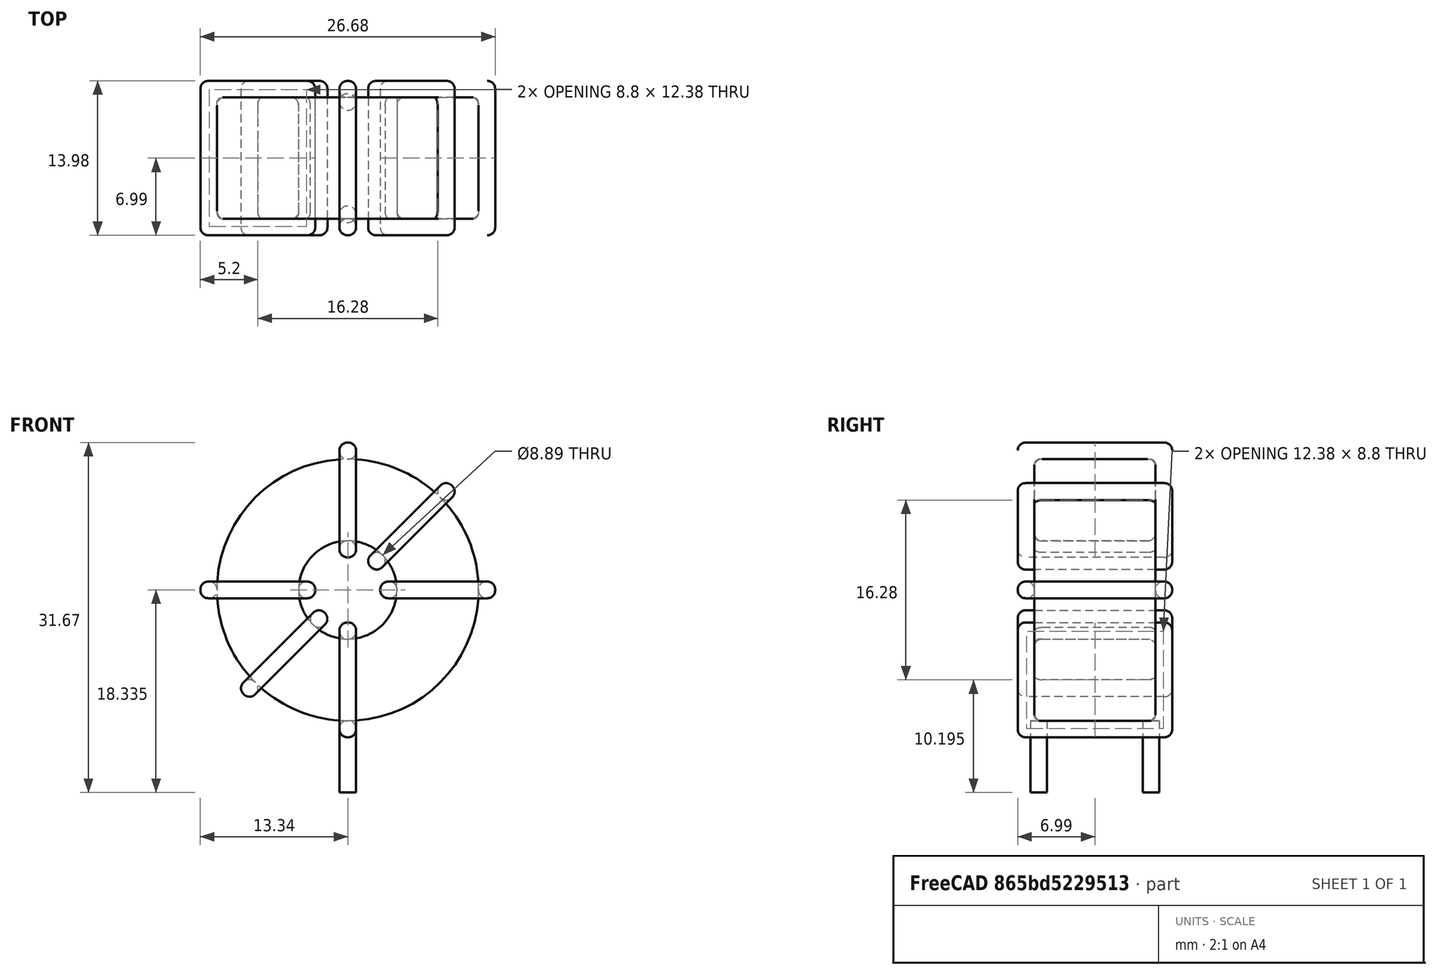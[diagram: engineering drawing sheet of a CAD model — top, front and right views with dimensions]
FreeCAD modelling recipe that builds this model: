
FCSTD DOCUMENT  (FreeCAD 0.16R6703 (Git))
Label: L_Toroid_Vertical_L26.7mm_W14.0mm_P10.16mm_Pulse_D
License: All rights reserved
LicenseURL: http://en.wikipedia.org/wiki/All_rights_reserved
objects: Sketcher::SketchObject×6, PartDesign::Pad×6, PartDesign::Fillet×5, Spreadsheet::Sheet×1
note: 23 computed .brp shape members not serialized (recipe doc carries the construction recipe); baked Part::Feature solids carry a one-line shape summary decoded from their .brp

FEATURE [Spreadsheet::Sheet] Spreadsheet  label="dimensions"
  cells = A1=Wx; B1(Wx)=26.67; C1(WW)=8.890000000000001; D1=26.67; A2=Wy; B2(Wy)=13.97; D2=13.97; A3=RM; B3(RMx)=10.16; C3(RMy)=0; A4=d_wire; B4(d_wire)=1.5; A5=H; B5(H)=26.67; A6=offsetx; B6(offsetx)=13.335
FEATURE [Sketcher::SketchObject] Sketch
  Placement = pos=(0,-5.08,0) rot=(1,0,0;1.5708rad)
  expr: Placement.Base.y = -Spreadsheet.RMx / 2
  expr: Constraints[0] = Spreadsheet.Wx / 2 - Spreadsheet.d_wire
  expr: Constraints[4] = Spreadsheet.WW / 2
  expr: Constraints[2] = Spreadsheet.Wx / 2 + Spreadsheet.d_wire + 0.5
  sketch-geometry (2):
    g0: Circle CenterX=0 CenterY=15.335 CenterZ=0 NormalX=0 NormalY=0 NormalZ=1 Radius=11.835
    g1: Circle CenterX=0 CenterY=15.335 CenterZ=0 NormalX=0 NormalY=0 NormalZ=1 Radius=4.445
  constraints (5):
    c: Radius(g0) = 11.835
    c: DistanceX(g-1,g0) = 0
    c: DistanceY(g-1,g0) = 15.335
    c: Coincident(g1,g0)
    c: Radius(g1) = 4.445
FEATURE [PartDesign::Pad] Pad
  Length = 10.97
  Length2 = 100
  Midplane = true
  Placement = pos=(0,-5.08,0) rot=(1,0,0;1.5708rad)
  Sketch = -> Sketch
  Type = 0
  expr: Length = Spreadsheet.Wy - 2 * Spreadsheet.d_wire
FEATURE [Sketcher::SketchObject] Sketch001
  Placement = pos=(0,0,2) rot=(0,0,1;0rad)
  expr: Placement.Base.z = 0.5 + Spreadsheet.d_wire
  expr: Constraints[4] = Spreadsheet.RMy
  expr: Constraints[2] = -Spreadsheet.RMx
  expr: Constraints[1] = Spreadsheet.d_wire / 2
  sketch-geometry (2):
    g0: Circle CenterX=0 CenterY=0 CenterZ=0 NormalX=0 NormalY=0 NormalZ=1 Radius=0.75
    g1: Circle CenterX=0 CenterY=-10.16 CenterZ=0 NormalX=0 NormalY=0 NormalZ=1 Radius=0.75
  constraints (5):
    c: Equal(g0,g1)
    c: Radius(g0) = 0.75
    c: DistanceY(g-1,g1) = -10.16
    c: Coincident(g0,g-1)
    c: DistanceX(g-1,g1) = 0
FEATURE [PartDesign::Pad] Pad001
  Length = 1.5
  Length2 = 5
  Placement = pos=(0,0,2) rot=(0,0,1;0rad)
  Reversed = true
  Sketch = -> Sketch001
  Type = 4
  expr: Length2 = 3.5 + Spreadsheet.d_wire
  expr: Length = Spreadsheet.d_wire
FEATURE [PartDesign::Fillet] Fillet
  Base = -> Pad [Edge6,Edge3,Edge2]
  Placement = pos=(0,-5.08,0) rot=(1,0,0;1.5708rad)
  Radius = 0.5
FEATURE [Sketcher::SketchObject] Sketch003
  Placement = pos=(0,1.905,15.335) rot=(1,0,0;3.14159rad)
  expr: Constraints[18] = Spreadsheet.d_wire
  expr: Constraints[16] = Spreadsheet.d_wire
  expr: Constraints[19] = Spreadsheet.d_wire
  expr: Constraints[17] = Spreadsheet.d_wire
  expr: Placement.Base.y = -1 * (Spreadsheet.RMx - Spreadsheet.Wy) / 2
  expr: Constraints[21] = (Spreadsheet.Wx - Spreadsheet.WW) / 2 - Spreadsheet.d_wire
  expr: Constraints[22] = Spreadsheet.Wx / 2 - Spreadsheet.d_wire
  expr: Constraints[43] = Spreadsheet.d_wire
  expr: Constraints[48] = Spreadsheet.Wx - Spreadsheet.d_wire * 2
  expr: Constraints[49] = Spreadsheet.Wy
  expr: Placement.Base.z = Spreadsheet.Wx / 2 + Spreadsheet.d_wire + 0.5
  sketch-geometry (16):
    g0: LineSegment StartX=-2.945 StartY=0 StartZ=0 EndX=-13.335 EndY=0 EndZ=0
    g1: LineSegment StartX=-13.335 StartY=0 StartZ=0 EndX=-13.335 EndY=13.97 EndZ=0
    g2: LineSegment StartX=-13.335 StartY=13.97 StartZ=0 EndX=-2.945 EndY=13.97 EndZ=0
    g3: LineSegment StartX=-2.945 StartY=13.97 StartZ=0 EndX=-2.945 EndY=0 EndZ=0
    g4: LineSegment StartX=-11.835 StartY=12.47 StartZ=0 EndX=-4.445 EndY=12.47 EndZ=0
    g5: LineSegment StartX=-4.445 StartY=12.47 StartZ=0 EndX=-4.445 EndY=1.5 EndZ=0
    g6: LineSegment StartX=-4.445 StartY=1.5 StartZ=0 EndX=-11.835 EndY=1.5 EndZ=0
    g7: LineSegment StartX=-11.835 StartY=1.5 StartZ=0 EndX=-11.835 EndY=12.47 EndZ=0
    g8: LineSegment StartX=2.945 StartY=13.97 StartZ=0 EndX=13.335 EndY=13.97 EndZ=0
    g9: LineSegment StartX=13.335 StartY=13.97 StartZ=0 EndX=13.335 EndY=0 EndZ=0
    g10: LineSegment StartX=13.335 StartY=0 StartZ=0 EndX=2.945 EndY=0 EndZ=0
    g11: LineSegment StartX=2.945 StartY=0 StartZ=0 EndX=2.945 EndY=13.97 EndZ=0
    g12: LineSegment StartX=4.445 StartY=12.47 StartZ=0 EndX=11.835 EndY=12.47 EndZ=0
    g13: LineSegment StartX=11.835 StartY=12.47 StartZ=0 EndX=11.835 EndY=1.5 EndZ=0
    g14: LineSegment StartX=11.835 StartY=1.5 StartZ=0 EndX=4.445 EndY=1.5 EndZ=0
    g15: LineSegment StartX=4.445 StartY=1.5 StartZ=0 EndX=4.445 EndY=12.47 EndZ=0
  constraints (50):
    c: Horizontal(g0)
    c: Coincident(g1,g0)
    c: Vertical(g1)
    c: Coincident(g2,g1)
    c: Horizontal(g2)
    c: Coincident(g3,g2)
    c: Coincident(g3,g0)
    c: Vertical(g3)
    c: Coincident(g4,g5)
    c: Coincident(g5,g6)
    c: Coincident(g6,g7)
    c: Coincident(g7,g4)
    c: Horizontal(g4)
    c: Horizontal(g6)
    c: Vertical(g5)
    c: Vertical(g7)
    c: DistanceX(g1,g4) = 1.5
    c: DistanceY(g4,g1) = 1.5
    c: DistanceX(g5,g0) = 1.5
    c: DistanceY(g0,g5) = 1.5
    c: DistanceY(g-1,g0) = 0
    c: DistanceX(g6,g6) = 7.39
    c: DistanceX(g6,g-1) = 11.835
    c: Coincident(g8,g9)
    c: Coincident(g9,g10)
    c: Coincident(g10,g11)
    c: Coincident(g11,g8)
    c: Horizontal(g8)
    c: Horizontal(g10)
    c: Vertical(g9)
    c: Vertical(g11)
    c: Coincident(g12,g13)
    c: Coincident(g13,g14)
    c: Coincident(g14,g15)
    c: Coincident(g15,g12)
    c: Horizontal(g12)
    c: Horizontal(g14)
    c: Vertical(g13)
    c: Vertical(g15)
    c: DistanceY(g8,g2) = 0
    c: DistanceY(g10,g0) = 0
    c: DistanceY(g14,g5) = 0
    c: DistanceY(g12,g4) = 0
    c: DistanceX(g8,g12) = 1.5
    c: Equal(g8,g2)
    c: Equal(g12,g4)
    c: Equal(g9,g1)
    c: Equal(g13,g7)
    c: DistanceX(g4,g12) = 23.67
    c: DistanceY(g0,g1) = 13.97
FEATURE [PartDesign::Pad] Pad002
  Length = 1.5
  Length2 = 100
  Midplane = true
  Placement = pos=(0,1.905,15.335) rot=(1,0,0;3.14159rad)
  Sketch = -> Sketch003
  Type = 0
  expr: Length = Spreadsheet.d_wire
FEATURE [PartDesign::Fillet] Fillet001
  Base = -> Pad002 [Edge38,Edge41,Edge42,Edge43,Edge29,Edge32,Edge33,Edge34,Edge25,Edge35,Edge36,Edge13,Edge14,Edge15,Edge16,Edge17,Edge18,Edge19,Edge1,Edge2,Edge3,Edge4,Edge5,Edge6,Edge7,Edge37,Edge39,Edge40,Edge20,Edge23,Edge24,Edge21,Edge22,Edge8,Edge9,Edge10,Edge11,Edge12,Edge26,Edge27,+8 more]
  Placement = pos=(0,1.905,15.335) rot=(1,0,0;3.14159rad)
  Radius = 0.705
  expr: Radius = Spreadsheet.d_wire * 0.47
FEATURE [Sketcher::SketchObject] Sketch004
  Placement = pos=(0,1.905,15.335) rot=(0.92388,0,0.382683;3.14159rad)
  expr: Constraints[18] = Spreadsheet.d_wire
  expr: Constraints[16] = Spreadsheet.d_wire
  expr: Constraints[19] = Spreadsheet.d_wire
  expr: Constraints[17] = Spreadsheet.d_wire
  expr: Placement.Base.y = -1 * (Spreadsheet.RMx - Spreadsheet.Wy) / 2
  expr: Constraints[21] = (Spreadsheet.Wx - Spreadsheet.WW) / 2 - Spreadsheet.d_wire
  expr: Constraints[22] = Spreadsheet.Wx / 2 - Spreadsheet.d_wire
  expr: Constraints[43] = Spreadsheet.d_wire
  expr: Constraints[48] = Spreadsheet.Wx - 2 * Spreadsheet.d_wire
  expr: Constraints[49] = Spreadsheet.Wy
  expr: Placement.Base.z = Spreadsheet.Wx / 2 + Spreadsheet.d_wire + 0.5
  sketch-geometry (16):
    g0: LineSegment StartX=-2.945 StartY=0 StartZ=0 EndX=-13.335 EndY=0 EndZ=0
    g1: LineSegment StartX=-13.335 StartY=0 StartZ=0 EndX=-13.335 EndY=13.97 EndZ=0
    g2: LineSegment StartX=-13.335 StartY=13.97 StartZ=0 EndX=-2.945 EndY=13.97 EndZ=0
    g3: LineSegment StartX=-2.945 StartY=13.97 StartZ=0 EndX=-2.945 EndY=0 EndZ=0
    g4: LineSegment StartX=-11.835 StartY=12.47 StartZ=0 EndX=-4.445 EndY=12.47 EndZ=0
    g5: LineSegment StartX=-4.445 StartY=12.47 StartZ=0 EndX=-4.445 EndY=1.5 EndZ=0
    g6: LineSegment StartX=-4.445 StartY=1.5 StartZ=0 EndX=-11.835 EndY=1.5 EndZ=0
    g7: LineSegment StartX=-11.835 StartY=1.5 StartZ=0 EndX=-11.835 EndY=12.47 EndZ=0
    g8: LineSegment StartX=2.945 StartY=13.97 StartZ=0 EndX=13.335 EndY=13.97 EndZ=0
    g9: LineSegment StartX=13.335 StartY=13.97 StartZ=0 EndX=13.335 EndY=0 EndZ=0
    g10: LineSegment StartX=13.335 StartY=0 StartZ=0 EndX=2.945 EndY=0 EndZ=0
    g11: LineSegment StartX=2.945 StartY=0 StartZ=0 EndX=2.945 EndY=13.97 EndZ=0
    g12: LineSegment StartX=4.445 StartY=12.47 StartZ=0 EndX=11.835 EndY=12.47 EndZ=0
    g13: LineSegment StartX=11.835 StartY=12.47 StartZ=0 EndX=11.835 EndY=1.5 EndZ=0
    g14: LineSegment StartX=11.835 StartY=1.5 StartZ=0 EndX=4.445 EndY=1.5 EndZ=0
    g15: LineSegment StartX=4.445 StartY=1.5 StartZ=0 EndX=4.445 EndY=12.47 EndZ=0
  constraints (50):
    c: Horizontal(g0)
    c: Coincident(g1,g0)
    c: Vertical(g1)
    c: Coincident(g2,g1)
    c: Horizontal(g2)
    c: Coincident(g3,g2)
    c: Coincident(g3,g0)
    c: Vertical(g3)
    c: Coincident(g4,g5)
    c: Coincident(g5,g6)
    c: Coincident(g6,g7)
    c: Coincident(g7,g4)
    c: Horizontal(g4)
    c: Horizontal(g6)
    c: Vertical(g5)
    c: Vertical(g7)
    c: DistanceX(g1,g4) = 1.5
    c: DistanceY(g4,g1) = 1.5
    c: DistanceX(g5,g0) = 1.5
    c: DistanceY(g0,g5) = 1.5
    c: DistanceY(g-1,g0) = 0
    c: DistanceX(g6,g6) = 7.39
    c: DistanceX(g6,g-1) = 11.835
    c: Coincident(g8,g9)
    c: Coincident(g9,g10)
    c: Coincident(g10,g11)
    c: Coincident(g11,g8)
    c: Horizontal(g8)
    c: Horizontal(g10)
    c: Vertical(g9)
    c: Vertical(g11)
    c: Coincident(g12,g13)
    c: Coincident(g13,g14)
    c: Coincident(g14,g15)
    c: Coincident(g15,g12)
    c: Horizontal(g12)
    c: Horizontal(g14)
    c: Vertical(g13)
    c: Vertical(g15)
    c: DistanceY(g8,g2) = 0
    c: DistanceY(g10,g0) = 0
    c: DistanceY(g14,g5) = 0
    c: DistanceY(g12,g4) = 0
    c: DistanceX(g8,g12) = 1.5
    c: Equal(g8,g2)
    c: Equal(g12,g4)
    c: Equal(g9,g1)
    c: Equal(g13,g7)
    c: DistanceX(g4,g12) = 23.67
    c: DistanceY(g0,g1) = 13.97
FEATURE [PartDesign::Pad] Pad003
  Length = 1.5
  Length2 = 100
  Midplane = true
  Placement = pos=(0,1.905,15.335) rot=(0.92388,0,0.382683;3.14159rad)
  Sketch = -> Sketch004
  Type = 0
  expr: Length = Spreadsheet.d_wire
FEATURE [PartDesign::Fillet] Fillet002
  Base = -> Pad003 [Edge38,Edge41,Edge42,Edge43,Edge29,Edge32,Edge33,Edge34,Edge25,Edge35,Edge36,Edge13,Edge14,Edge15,Edge16,Edge17,Edge18,Edge19,Edge1,Edge2,Edge3,Edge4,Edge5,Edge6,Edge7,Edge37,Edge39,Edge40,Edge20,Edge23,Edge24,Edge21,Edge22,Edge8,Edge9,Edge10,Edge11,Edge12,Edge26,Edge27,+8 more]
  Placement = pos=(0,1.905,15.335) rot=(0.92388,0,0.382683;3.14159rad)
  Radius = 0.705
  expr: Radius = Spreadsheet.d_wire * 0.47
FEATURE [Sketcher::SketchObject] Sketch005
  Placement = pos=(0,1.905,15.335) rot=(0.92388,0,-0.382683;3.14159rad)
  expr: Constraints[18] = Spreadsheet.d_wire
  expr: Constraints[16] = Spreadsheet.d_wire
  expr: Constraints[19] = Spreadsheet.d_wire
  expr: Constraints[17] = Spreadsheet.d_wire
  expr: Placement.Base.y = -1 * (Spreadsheet.RMx - Spreadsheet.Wy) / 2
  expr: Constraints[21] = (Spreadsheet.Wx - Spreadsheet.WW) / 2 - Spreadsheet.d_wire
  expr: Constraints[22] = Spreadsheet.Wx / 2 - Spreadsheet.d_wire
  expr: Constraints[43] = Spreadsheet.d_wire
  expr: Constraints[48] = Spreadsheet.Wx - 2 * Spreadsheet.d_wire
  expr: Constraints[49] = Spreadsheet.Wy
  expr: Placement.Base.z = Spreadsheet.Wx / 2 + Spreadsheet.d_wire + 0.5
  sketch-geometry (16):
    g0: LineSegment StartX=-2.945 StartY=0 StartZ=0 EndX=-13.335 EndY=0 EndZ=0
    g1: LineSegment StartX=-13.335 StartY=0 StartZ=0 EndX=-13.335 EndY=13.97 EndZ=0
    g2: LineSegment StartX=-13.335 StartY=13.97 StartZ=0 EndX=-2.945 EndY=13.97 EndZ=0
    g3: LineSegment StartX=-2.945 StartY=13.97 StartZ=0 EndX=-2.945 EndY=0 EndZ=0
    g4: LineSegment StartX=-11.835 StartY=12.47 StartZ=0 EndX=-4.445 EndY=12.47 EndZ=0
    g5: LineSegment StartX=-4.445 StartY=12.47 StartZ=0 EndX=-4.445 EndY=1.5 EndZ=0
    g6: LineSegment StartX=-4.445 StartY=1.5 StartZ=0 EndX=-11.835 EndY=1.5 EndZ=0
    g7: LineSegment StartX=-11.835 StartY=1.5 StartZ=0 EndX=-11.835 EndY=12.47 EndZ=0
    g8: LineSegment StartX=2.945 StartY=13.97 StartZ=0 EndX=13.335 EndY=13.97 EndZ=0
    g9: LineSegment StartX=13.335 StartY=13.97 StartZ=0 EndX=13.335 EndY=0 EndZ=0
    g10: LineSegment StartX=13.335 StartY=0 StartZ=0 EndX=2.945 EndY=0 EndZ=0
    g11: LineSegment StartX=2.945 StartY=0 StartZ=0 EndX=2.945 EndY=13.97 EndZ=0
    g12: LineSegment StartX=4.445 StartY=12.47 StartZ=0 EndX=11.835 EndY=12.47 EndZ=0
    g13: LineSegment StartX=11.835 StartY=12.47 StartZ=0 EndX=11.835 EndY=1.5 EndZ=0
    g14: LineSegment StartX=11.835 StartY=1.5 StartZ=0 EndX=4.445 EndY=1.5 EndZ=0
    g15: LineSegment StartX=4.445 StartY=1.5 StartZ=0 EndX=4.445 EndY=12.47 EndZ=0
  constraints (50):
    c: Horizontal(g0)
    c: Coincident(g1,g0)
    c: Vertical(g1)
    c: Coincident(g2,g1)
    c: Horizontal(g2)
    c: Coincident(g3,g2)
    c: Coincident(g3,g0)
    c: Vertical(g3)
    c: Coincident(g4,g5)
    c: Coincident(g5,g6)
    c: Coincident(g6,g7)
    c: Coincident(g7,g4)
    c: Horizontal(g4)
    c: Horizontal(g6)
    c: Vertical(g5)
    c: Vertical(g7)
    c: DistanceX(g1,g4) = 1.5
    c: DistanceY(g4,g1) = 1.5
    c: DistanceX(g5,g0) = 1.5
    c: DistanceY(g0,g5) = 1.5
    c: DistanceY(g-1,g0) = 0
    c: DistanceX(g6,g6) = 7.39
    c: DistanceX(g6,g-1) = 11.835
    c: Coincident(g8,g9)
    c: Coincident(g9,g10)
    c: Coincident(g10,g11)
    c: Coincident(g11,g8)
    c: Horizontal(g8)
    c: Horizontal(g10)
    c: Vertical(g9)
    c: Vertical(g11)
    c: Coincident(g12,g13)
    c: Coincident(g13,g14)
    c: Coincident(g14,g15)
    c: Coincident(g15,g12)
    c: Horizontal(g12)
    c: Horizontal(g14)
    c: Vertical(g13)
    c: Vertical(g15)
    c: DistanceY(g8,g2) = 0
    c: DistanceY(g10,g0) = 0
    c: DistanceY(g14,g5) = 0
    c: DistanceY(g12,g4) = 0
    c: DistanceX(g8,g12) = 1.5
    c: Equal(g8,g2)
    c: Equal(g12,g4)
    c: Equal(g9,g1)
    c: Equal(g13,g7)
    c: DistanceX(g4,g12) = 23.67
    c: DistanceY(g0,g1) = 13.97
FEATURE [PartDesign::Pad] Pad004
  Length = 1.5
  Length2 = 100
  Midplane = true
  Placement = pos=(0,1.905,15.335) rot=(0.92388,0,-0.382683;3.14159rad)
  Sketch = -> Sketch005
  Type = 0
  expr: Length = Spreadsheet.d_wire
FEATURE [PartDesign::Fillet] Fillet003
  Base = -> Pad004 [Edge38,Edge41,Edge42,Edge43,Edge29,Edge32,Edge33,Edge34,Edge25,Edge35,Edge36,Edge13,Edge14,Edge15,Edge16,Edge17,Edge18,Edge19,Edge1,Edge2,Edge3,Edge4,Edge5,Edge6,Edge7,Edge37,Edge39,Edge40,Edge20,Edge23,Edge24,Edge21,Edge22,Edge8,Edge9,Edge10,Edge11,Edge12,Edge26,Edge27,+8 more]
  Placement = pos=(0,1.905,15.335) rot=(0.92388,0,-0.382683;3.14159rad)
  Radius = 0.705
  expr: Radius = Spreadsheet.d_wire * 0.47
FEATURE [Sketcher::SketchObject] Sketch006
  Placement = pos=(0,1.905,15.335) rot=(0.707107,0,0.707107;3.14159rad)
  expr: Constraints[18] = Spreadsheet.d_wire
  expr: Constraints[16] = Spreadsheet.d_wire
  expr: Constraints[19] = Spreadsheet.d_wire
  expr: Constraints[17] = Spreadsheet.d_wire
  expr: Placement.Base.y = -1 * (Spreadsheet.RMx - Spreadsheet.Wy) / 2
  expr: Constraints[21] = (Spreadsheet.Wx - Spreadsheet.WW) / 2 - Spreadsheet.d_wire
  expr: Constraints[22] = Spreadsheet.Wx / 2 - Spreadsheet.d_wire
  expr: Constraints[43] = Spreadsheet.d_wire
  expr: Constraints[48] = Spreadsheet.Wx - Spreadsheet.d_wire * 2
  expr: Constraints[49] = Spreadsheet.Wy
  expr: Placement.Base.z = Spreadsheet.Wx / 2 + Spreadsheet.d_wire + 0.5
  sketch-geometry (16):
    g0: LineSegment StartX=-2.945 StartY=0 StartZ=0 EndX=-13.335 EndY=0 EndZ=0
    g1: LineSegment StartX=-13.335 StartY=0 StartZ=0 EndX=-13.335 EndY=13.97 EndZ=0
    g2: LineSegment StartX=-13.335 StartY=13.97 StartZ=0 EndX=-2.945 EndY=13.97 EndZ=0
    g3: LineSegment StartX=-2.945 StartY=13.97 StartZ=0 EndX=-2.945 EndY=0 EndZ=0
    g4: LineSegment StartX=-11.835 StartY=12.47 StartZ=0 EndX=-4.445 EndY=12.47 EndZ=0
    g5: LineSegment StartX=-4.445 StartY=12.47 StartZ=0 EndX=-4.445 EndY=1.5 EndZ=0
    g6: LineSegment StartX=-4.445 StartY=1.5 StartZ=0 EndX=-11.835 EndY=1.5 EndZ=0
    g7: LineSegment StartX=-11.835 StartY=1.5 StartZ=0 EndX=-11.835 EndY=12.47 EndZ=0
    g8: LineSegment StartX=2.945 StartY=13.97 StartZ=0 EndX=13.335 EndY=13.97 EndZ=0
    g9: LineSegment StartX=13.335 StartY=13.97 StartZ=0 EndX=13.335 EndY=0 EndZ=0
    g10: LineSegment StartX=13.335 StartY=0 StartZ=0 EndX=2.945 EndY=0 EndZ=0
    g11: LineSegment StartX=2.945 StartY=0 StartZ=0 EndX=2.945 EndY=13.97 EndZ=0
    g12: LineSegment StartX=4.445 StartY=12.47 StartZ=0 EndX=11.835 EndY=12.47 EndZ=0
    g13: LineSegment StartX=11.835 StartY=12.47 StartZ=0 EndX=11.835 EndY=1.5 EndZ=0
    g14: LineSegment StartX=11.835 StartY=1.5 StartZ=0 EndX=4.445 EndY=1.5 EndZ=0
    g15: LineSegment StartX=4.445 StartY=1.5 StartZ=0 EndX=4.445 EndY=12.47 EndZ=0
  constraints (50):
    c: Horizontal(g0)
    c: Coincident(g1,g0)
    c: Vertical(g1)
    c: Coincident(g2,g1)
    c: Horizontal(g2)
    c: Coincident(g3,g2)
    c: Coincident(g3,g0)
    c: Vertical(g3)
    c: Coincident(g4,g5)
    c: Coincident(g5,g6)
    c: Coincident(g6,g7)
    c: Coincident(g7,g4)
    c: Horizontal(g4)
    c: Horizontal(g6)
    c: Vertical(g5)
    c: Vertical(g7)
    c: DistanceX(g1,g4) = 1.5
    c: DistanceY(g4,g1) = 1.5
    c: DistanceX(g5,g0) = 1.5
    c: DistanceY(g0,g5) = 1.5
    c: DistanceY(g-1,g0) = 0
    c: DistanceX(g6,g6) = 7.39
    c: DistanceX(g6,g-1) = 11.835
    c: Coincident(g8,g9)
    c: Coincident(g9,g10)
    c: Coincident(g10,g11)
    c: Coincident(g11,g8)
    c: Horizontal(g8)
    c: Horizontal(g10)
    c: Vertical(g9)
    c: Vertical(g11)
    c: Coincident(g12,g13)
    c: Coincident(g13,g14)
    c: Coincident(g14,g15)
    c: Coincident(g15,g12)
    c: Horizontal(g12)
    c: Horizontal(g14)
    c: Vertical(g13)
    c: Vertical(g15)
    c: DistanceY(g8,g2) = 0
    c: DistanceY(g10,g0) = 0
    c: DistanceY(g14,g5) = 0
    c: DistanceY(g12,g4) = 0
    c: DistanceX(g8,g12) = 1.5
    c: Equal(g8,g2)
    c: Equal(g12,g4)
    c: Equal(g9,g1)
    c: Equal(g13,g7)
    c: DistanceX(g4,g12) = 23.67
    c: DistanceY(g0,g1) = 13.97
FEATURE [PartDesign::Pad] Pad005
  Length = 1.5
  Length2 = 100
  Midplane = true
  Placement = pos=(0,1.905,15.335) rot=(0.707107,0,0.707107;3.14159rad)
  Sketch = -> Sketch006
  Type = 0
  expr: Length = Spreadsheet.d_wire
FEATURE [PartDesign::Fillet] Fillet004
  Base = -> Pad005 [Edge38,Edge41,Edge42,Edge43,Edge29,Edge32,Edge33,Edge34,Edge25,Edge35,Edge36,Edge13,Edge14,Edge15,Edge16,Edge17,Edge18,Edge19,Edge1,Edge2,Edge3,Edge4,Edge5,Edge6,Edge7,Edge37,Edge39,Edge40,Edge20,Edge23,Edge24,Edge21,Edge22,Edge8,Edge9,Edge10,Edge11,Edge12,Edge26,Edge27,+8 more]
  Placement = pos=(0,1.905,15.335) rot=(0.707107,0,0.707107;3.14159rad)
  Radius = 0.705
  expr: Radius = Spreadsheet.d_wire * 0.47
